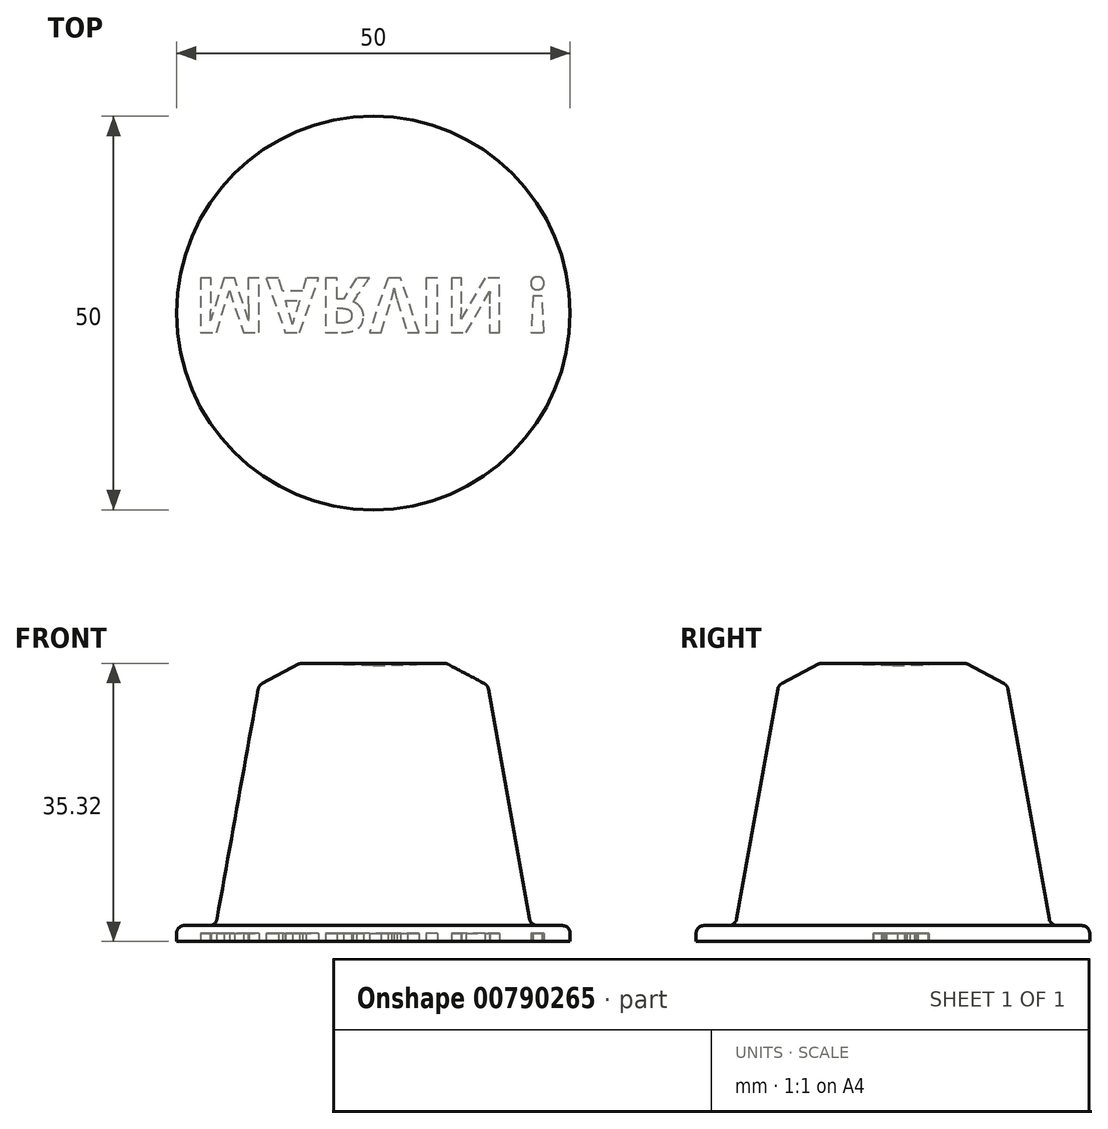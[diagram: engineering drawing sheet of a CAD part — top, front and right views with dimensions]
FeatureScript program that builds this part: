
annotation { "Feature Type Name" : "Feature", "Feature Type Description" : "" }
export const myFeature = defineFeature(function(context is Context, id is Id, definition is map)
    precondition{}
    {
        {
            var Q0;
            Q0=qCreatedBy(makeId("Front.planeOp"),FACE);
            var sketch = newSketch(context, id + "F0", { "sketchPlane" : qUnion([Q0])});
            skLineSegment(sketch, "E0", {"start": v(-25, 26.53) * mm, "end": v(-25, -8.47) * mm});
            skLineSegment(sketch, "E1", {"start": v(-25, -8.47) * mm, "end": v(0, -8.47) * mm});
            skLineSegment(sketch, "E2", {"start": v(0, -8.47) * mm, "end": v(0, -6.47) * mm});
            skLineSegment(sketch, "E3", {"start": v(0, -6.47) * mm, "end": v(-5, -6.47) * mm});
            skLineSegment(sketch, "E4", {"start": v(-15.76, 26.86) * mm, "end": v(-25, 26.53) * mm});
            skLineSegment(sketch, "E5", {"start": v(-5, -6.47) * mm, "end": v(-10.46, 24.05) * mm});
            skLineSegment(sketch, "E6", {"start": v(-10.46, 24.05) * mm, "end": v(-15.76, 26.86) * mm});
            skSolve(sketch);
        }
        {
            var Q0;
            Q0=makeQuery(id+"F0.imprint","IMPRINT",FACE,{"disambiguationData":[TD([[makeQuery(id+"F0.imprint","IMPRINT",EDGE,{"derivedFrom":sQuery(id+"F0.wireOp",EDGE,"E0")}),1.0]])]});
            var Q1;
            Q1=sQuery(id+"F0.wireOp",EDGE,"E0");
            revolve(context, id + "F1", {"surfaceOperationType" : NewSurfaceOperationType.NEW, "entities" : qUnion([Q0]), "axis" : qUnion([Q1]), "revolveType" : RevolveType.FULL});
        }
        {
            var Q0;
            Q0=makeQuery(id+"F1.opRevolve","SWEPT_EDGE",EDGE,{"disambiguationData":[OSD([sQuery(id+"F0.wireOp",EDGE,"E2"),sQuery(id+"F0.wireOp",EDGE,"E3")])]});
            fillet(context, id + "F2", {"entities" : qUnion([Q0]), "radius" : 1 * mm, "tangentPropagation" : true, "allowEdgeOverflow" : false});
        }
        {
            var Q0;
            Q0=makeQuery(id+"F1.opRevolve","SWEPT_EDGE",EDGE,{"disambiguationData":[OSD([sQuery(id+"F0.wireOp",EDGE,"E5"),sQuery(id+"F0.wireOp",EDGE,"E6")])]});
            fillet(context, id + "F3", {"entities" : qUnion([Q0]), "radius" : 1 * mm, "tangentPropagation" : true, "allowEdgeOverflow" : false});
        }
        {
            var Q0;
            Q0=makeQuery(id+"F1.opRevolve","SWEPT_EDGE",EDGE,{"disambiguationData":[OSD([sQuery(id+"F0.wireOp",EDGE,"E4"),sQuery(id+"F0.wireOp",EDGE,"E6")])]});
            fillet(context, id + "F4", {"entities" : qUnion([Q0]), "radius" : 1 * mm, "tangentPropagation" : true, "allowEdgeOverflow" : false});
        }
        {
            var Q0;
            Q0=makeQuery(id+"F1.opRevolve","SWEPT_FACE",FACE,{"disambiguationData":[OSD([sQuery(id+"F0.wireOp",EDGE,"E1")])]});
            var sketch = newSketch(context, id + "F5", { "sketchPlane" : qUnion([Q0])});
            skLineSegment(sketch, "E7", {"start": v(-25.12, 12.7) * mm, "end": v(-25.12, -12.7) * mm});
            skText(sketch, "E8", { "text": "MARVIN !", "fontName": "OpenSans-Bold.ttf"});
            const initialGuessF5  = {"E8": [-0.0478, -0.00446, 1, 0, 0.007]};
            skSetInitialGuess(sketch, initialGuessF5);
            skSolve(sketch);
        }
        {
            var Q0;
            Q0=makeQuery(id+"F1.opRevolve","SWEPT_EDGE",EDGE,{"disambiguationData":[OSD([sQuery(id+"F0.wireOp",EDGE,"E3"),sQuery(id+"F0.wireOp",EDGE,"E5")])]});
            fillet(context, id + "F6", {"entities" : qUnion([Q0]), "radius" : 1 * mm, "tangentPropagation" : true, "allowEdgeOverflow" : false});
        }
        {
            var Q0;
            Q0 = qSketchRegion(id + "F5", true);
            extrude(context, id + "F7", {"entities" : qUnion([Q0]), "operationType" : NewBodyOperationType.REMOVE, "oppositeDirection" : true, "depth" : 1 * mm, "offsetDistance" : 25 * mm});
        }
    });
